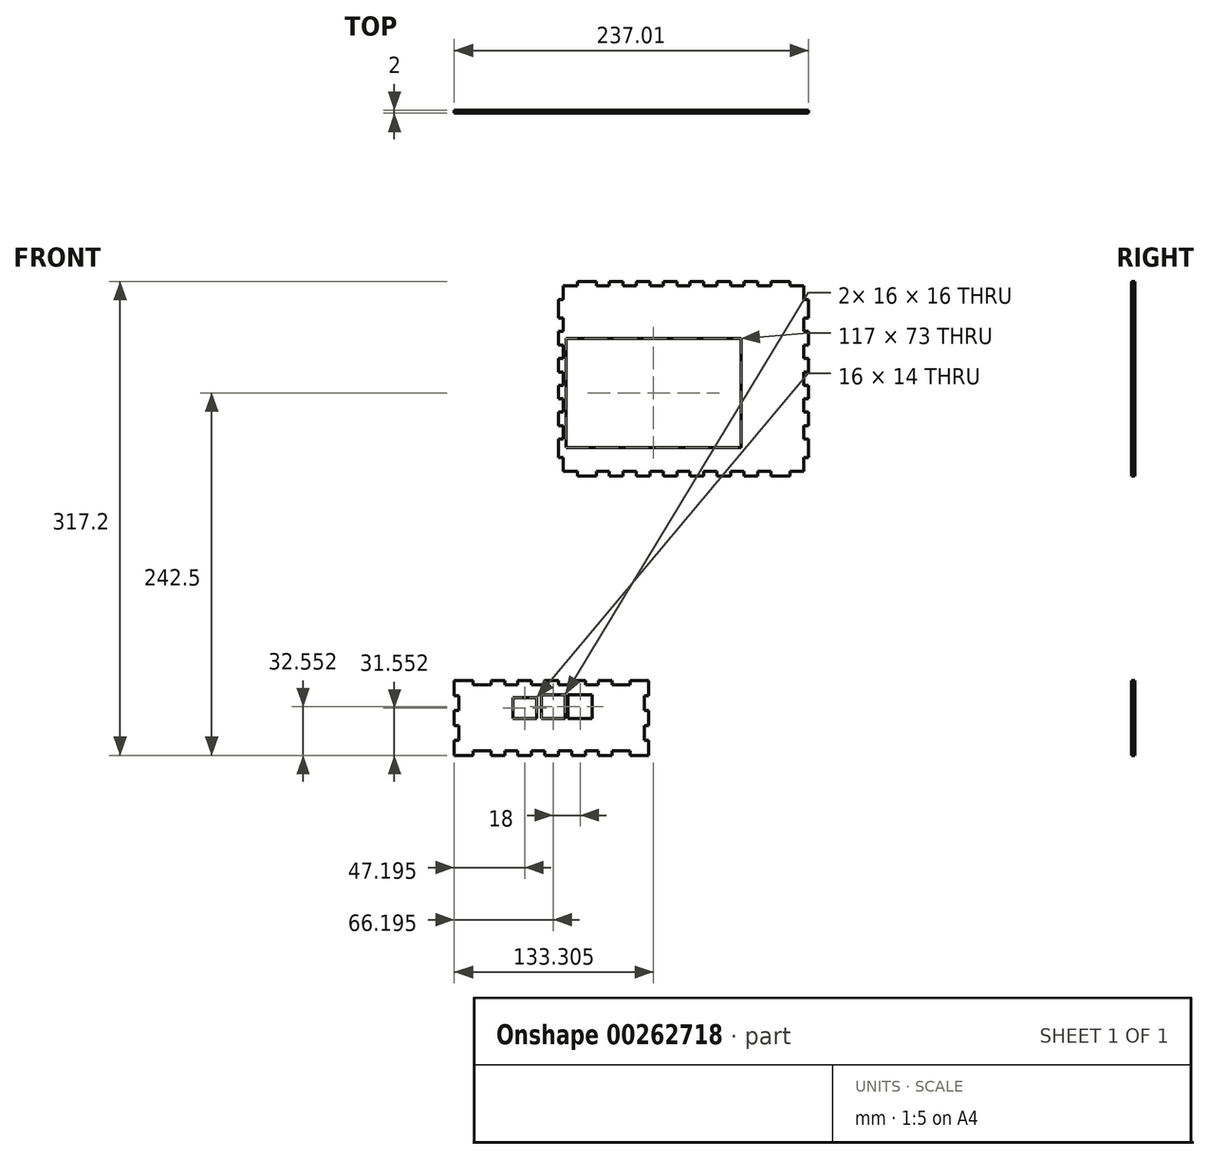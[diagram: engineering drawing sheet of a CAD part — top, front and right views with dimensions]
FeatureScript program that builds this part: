
annotation { "Feature Type Name" : "Feature", "Feature Type Description" : "" }
export const myFeature = defineFeature(function(context is Context, id is Id, definition is map)
    precondition{}
    {
        {
            var Q0;
            Q0=qCreatedBy(makeId("Front.planeOp"),FACE);
            var sketch = newSketch(context, id + "F0", { "sketchPlane" : qUnion([Q0])});
            skLineSegment(sketch, "E0.bottom", {"start": v(-364.73, 294.66) * mm, "end": v(-247.73, 294.66) * mm});
            skLineSegment(sketch, "E0.top", {"start": v(-364.73, 221.66) * mm, "end": v(-247.73, 221.66) * mm});
            skLineSegment(sketch, "E0.left", {"start": v(-364.73, 294.66) * mm, "end": v(-364.73, 221.66) * mm});
            skLineSegment(sketch, "E0.right", {"start": v(-247.73, 294.66) * mm, "end": v(-247.73, 221.66) * mm});
            skLineSegment(sketch, "E1.bottom", {"start": v(-103.23, 148.82) * mm, "end": v(61.85, 148.82) * mm});
            skLineSegment(sketch, "E1.top", {"start": v(-103.23, 18.82) * mm, "end": v(61.85, 18.82) * mm});
            skLineSegment(sketch, "E1.left", {"start": v(-103.23, 148.82) * mm, "end": v(-103.23, 18.82) * mm});
            skLineSegment(sketch, "E1.right", {"start": v(61.85, 148.82) * mm, "end": v(61.85, 18.82) * mm});
            skLineSegment(sketch, "E2", {"start": v(-298.1, 53.2) * mm, "end": v(-285.64, 53.2) * mm});
            skLineSegment(sketch, "E3", {"start": v(-285.64, 53.2) * mm, "end": v(-285.64, 50.2) * mm});
            skLineSegment(sketch, "E4", {"start": v(-285.64, 50.2) * mm, "end": v(-273.6, 50.2) * mm});
            skLineSegment(sketch, "E5", {"start": v(-273.6, 50.2) * mm, "end": v(-273.6, 53.2) * mm});
            skLineSegment(sketch, "E6", {"start": v(-273.6, 53.2) * mm, "end": v(-264.4, 53.2) * mm});
            skLineSegment(sketch, "E7", {"start": v(-264.4, 53.2) * mm, "end": v(-264.4, 50.2) * mm});
            skLineSegment(sketch, "E8", {"start": v(-264.4, 50.2) * mm, "end": v(-255.6, 50.2) * mm});
            skLineSegment(sketch, "E9", {"start": v(-255.6, 50.2) * mm, "end": v(-255.6, 53.2) * mm});
            skLineSegment(sketch, "E10", {"start": v(-255.6, 53.2) * mm, "end": v(-246.4, 53.2) * mm});
            skLineSegment(sketch, "E11", {"start": v(-246.4, 53.2) * mm, "end": v(-246.4, 50.2) * mm});
            skLineSegment(sketch, "E12", {"start": v(-246.4, 50.2) * mm, "end": v(-237.6, 50.2) * mm});
            skLineSegment(sketch, "E13", {"start": v(-237.6, 50.2) * mm, "end": v(-237.6, 53.2) * mm});
            skLineSegment(sketch, "E14", {"start": v(-237.6, 53.2) * mm, "end": v(-228.4, 53.2) * mm});
            skLineSegment(sketch, "E15", {"start": v(-228.4, 53.2) * mm, "end": v(-228.4, 50.2) * mm});
            skLineSegment(sketch, "E16", {"start": v(-228.4, 50.2) * mm, "end": v(-219.6, 50.2) * mm});
            skLineSegment(sketch, "E17", {"start": v(-219.6, 50.2) * mm, "end": v(-219.6, 53.2) * mm});
            skLineSegment(sketch, "E18", {"start": v(-219.6, 53.2) * mm, "end": v(-210.4, 53.2) * mm});
            skLineSegment(sketch, "E19", {"start": v(-210.4, 53.2) * mm, "end": v(-210.4, 50.2) * mm});
            skLineSegment(sketch, "E20", {"start": v(-210.4, 50.2) * mm, "end": v(-201.6, 50.2) * mm});
            skLineSegment(sketch, "E21", {"start": v(-201.6, 50.2) * mm, "end": v(-201.6, 53.2) * mm});
            skLineSegment(sketch, "E22", {"start": v(-201.6, 53.2) * mm, "end": v(-192.4, 53.2) * mm});
            skLineSegment(sketch, "E23", {"start": v(-192.4, 53.2) * mm, "end": v(-192.4, 50.2) * mm});
            skLineSegment(sketch, "E24", {"start": v(-192.4, 50.2) * mm, "end": v(-180.34, 50.2) * mm});
            skLineSegment(sketch, "E25", {"start": v(-180.34, 50.2) * mm, "end": v(-180.34, 53.2) * mm});
            skLineSegment(sketch, "E26", {"start": v(-180.34, 53.2) * mm, "end": v(-167.9, 53.2) * mm});
            skLineSegment(sketch, "E27", {"start": v(-167.9, 53.2) * mm, "end": v(-167.9, 43) * mm});
            skLineSegment(sketch, "E28", {"start": v(-167.9, 43) * mm, "end": v(-170.9, 43) * mm});
            skLineSegment(sketch, "E29", {"start": v(-170.9, 43) * mm, "end": v(-170.9, 33.2) * mm});
            skLineSegment(sketch, "E30", {"start": v(-170.9, 33.2) * mm, "end": v(-167.9, 33.2) * mm});
            skLineSegment(sketch, "E31", {"start": v(-167.9, 33.2) * mm, "end": v(-167.9, 23) * mm});
            skLineSegment(sketch, "E32", {"start": v(-167.9, 23) * mm, "end": v(-170.9, 23) * mm});
            skLineSegment(sketch, "E33", {"start": v(-170.9, 23) * mm, "end": v(-170.9, 13.2) * mm});
            skLineSegment(sketch, "E34", {"start": v(-170.9, 13.2) * mm, "end": v(-167.9, 13.2) * mm});
            skLineSegment(sketch, "E35", {"start": v(-167.9, 13.2) * mm, "end": v(-167.9, 3) * mm});
            skLineSegment(sketch, "E36", {"start": v(-167.9, 3) * mm, "end": v(-180.34, 3) * mm});
            skLineSegment(sketch, "E37", {"start": v(-180.34, 3) * mm, "end": v(-180.34, 6) * mm});
            skLineSegment(sketch, "E38", {"start": v(-180.34, 6) * mm, "end": v(-192.4, 6) * mm});
            skLineSegment(sketch, "E39", {"start": v(-192.4, 6) * mm, "end": v(-192.4, 3) * mm});
            skLineSegment(sketch, "E40", {"start": v(-192.4, 3) * mm, "end": v(-201.6, 3) * mm});
            skLineSegment(sketch, "E41", {"start": v(-201.6, 3) * mm, "end": v(-201.6, 6) * mm});
            skLineSegment(sketch, "E42", {"start": v(-201.6, 6) * mm, "end": v(-210.4, 6) * mm});
            skLineSegment(sketch, "E43", {"start": v(-210.4, 6) * mm, "end": v(-210.4, 3) * mm});
            skLineSegment(sketch, "E44", {"start": v(-210.4, 3) * mm, "end": v(-219.6, 3) * mm});
            skLineSegment(sketch, "E45", {"start": v(-219.6, 3) * mm, "end": v(-219.6, 6) * mm});
            skLineSegment(sketch, "E46", {"start": v(-219.6, 6) * mm, "end": v(-228.4, 6) * mm});
            skLineSegment(sketch, "E47", {"start": v(-228.4, 6) * mm, "end": v(-228.4, 3) * mm});
            skLineSegment(sketch, "E48", {"start": v(-228.4, 3) * mm, "end": v(-237.6, 3) * mm});
            skLineSegment(sketch, "E49", {"start": v(-237.6, 3) * mm, "end": v(-237.6, 6) * mm});
            skLineSegment(sketch, "E50", {"start": v(-237.6, 6) * mm, "end": v(-246.4, 6) * mm});
            skLineSegment(sketch, "E51", {"start": v(-246.4, 6) * mm, "end": v(-246.4, 3) * mm});
            skLineSegment(sketch, "E52", {"start": v(-246.4, 3) * mm, "end": v(-255.6, 3) * mm});
            skLineSegment(sketch, "E53", {"start": v(-255.6, 3) * mm, "end": v(-255.6, 6) * mm});
            skLineSegment(sketch, "E54", {"start": v(-255.6, 6) * mm, "end": v(-264.4, 6) * mm});
            skLineSegment(sketch, "E55", {"start": v(-264.4, 6) * mm, "end": v(-264.4, 3) * mm});
            skLineSegment(sketch, "E56", {"start": v(-264.4, 3) * mm, "end": v(-273.6, 3) * mm});
            skLineSegment(sketch, "E57", {"start": v(-273.6, 3) * mm, "end": v(-273.6, 6) * mm});
            skLineSegment(sketch, "E58", {"start": v(-273.6, 6) * mm, "end": v(-285.64, 6) * mm});
            skLineSegment(sketch, "E59", {"start": v(-285.64, 6) * mm, "end": v(-285.64, 3) * mm});
            skLineSegment(sketch, "E60", {"start": v(-285.64, 3) * mm, "end": v(-298.1, 3) * mm});
            skLineSegment(sketch, "E61", {"start": v(-298.1, 3) * mm, "end": v(-298.1, 13.2) * mm});
            skLineSegment(sketch, "E62", {"start": v(-298.1, 13.2) * mm, "end": v(-295.1, 13.2) * mm});
            skLineSegment(sketch, "E63", {"start": v(-295.1, 13.2) * mm, "end": v(-295.1, 23) * mm});
            skLineSegment(sketch, "E64", {"start": v(-295.1, 23) * mm, "end": v(-298.1, 23) * mm});
            skLineSegment(sketch, "E65", {"start": v(-298.1, 23) * mm, "end": v(-298.1, 33.2) * mm});
            skLineSegment(sketch, "E66", {"start": v(-298.1, 33.2) * mm, "end": v(-295.1, 33.2) * mm});
            skLineSegment(sketch, "E67", {"start": v(-295.1, 33.2) * mm, "end": v(-295.1, 43) * mm});
            skLineSegment(sketch, "E68", {"start": v(-295.1, 43) * mm, "end": v(-298.1, 43) * mm});
            skLineSegment(sketch, "E69", {"start": v(-298.1, 43) * mm, "end": v(-298.1, 53.2) * mm});
            skLineSegment(sketch, "E70", {"start": v(-225.28, 193) * mm, "end": v(-225.28, 202.25) * mm});
            skLineSegment(sketch, "E71", {"start": v(-225.28, 202.25) * mm, "end": v(-228.28, 202.25) * mm});
            skLineSegment(sketch, "E72", {"start": v(-228.28, 202.25) * mm, "end": v(-228.28, 214.7) * mm});
            skLineSegment(sketch, "E73", {"start": v(-228.28, 214.7) * mm, "end": v(-225.28, 214.7) * mm});
            skLineSegment(sketch, "E74", {"start": v(-225.28, 214.7) * mm, "end": v(-225.28, 223.5) * mm});
            skLineSegment(sketch, "E75", {"start": v(-225.28, 223.5) * mm, "end": v(-228.28, 223.5) * mm});
            skLineSegment(sketch, "E76", {"start": v(-228.28, 223.5) * mm, "end": v(-228.28, 232.7) * mm});
            skLineSegment(sketch, "E77", {"start": v(-228.28, 232.7) * mm, "end": v(-225.28, 232.7) * mm});
            skLineSegment(sketch, "E78", {"start": v(-225.28, 232.7) * mm, "end": v(-225.28, 241.5) * mm});
            skLineSegment(sketch, "E79", {"start": v(-225.28, 241.5) * mm, "end": v(-228.28, 241.5) * mm});
            skLineSegment(sketch, "E80", {"start": v(-228.28, 241.5) * mm, "end": v(-228.28, 250.7) * mm});
            skLineSegment(sketch, "E81", {"start": v(-228.28, 250.7) * mm, "end": v(-225.28, 250.7) * mm});
            skLineSegment(sketch, "E82", {"start": v(-225.28, 250.7) * mm, "end": v(-225.28, 259.5) * mm});
            skLineSegment(sketch, "E83", {"start": v(-225.28, 259.5) * mm, "end": v(-228.28, 259.5) * mm});
            skLineSegment(sketch, "E84", {"start": v(-228.28, 259.5) * mm, "end": v(-228.28, 268.7) * mm});
            skLineSegment(sketch, "E85", {"start": v(-228.28, 268.7) * mm, "end": v(-225.28, 268.7) * mm});
            skLineSegment(sketch, "E86", {"start": v(-225.28, 268.7) * mm, "end": v(-225.28, 277.5) * mm});
            skLineSegment(sketch, "E87", {"start": v(-225.28, 277.5) * mm, "end": v(-228.28, 277.5) * mm});
            skLineSegment(sketch, "E88", {"start": v(-228.28, 277.5) * mm, "end": v(-228.28, 286.7) * mm});
            skLineSegment(sketch, "E89", {"start": v(-228.28, 286.7) * mm, "end": v(-225.28, 286.7) * mm});
            skLineSegment(sketch, "E90", {"start": v(-225.28, 286.7) * mm, "end": v(-225.28, 295.5) * mm});
            skLineSegment(sketch, "E91", {"start": v(-225.28, 295.5) * mm, "end": v(-228.28, 295.5) * mm});
            skLineSegment(sketch, "E92", {"start": v(-228.28, 295.5) * mm, "end": v(-228.28, 307.95) * mm});
            skLineSegment(sketch, "E93", {"start": v(-228.28, 307.95) * mm, "end": v(-225.28, 307.95) * mm});
            skLineSegment(sketch, "E94", {"start": v(-225.28, 307.95) * mm, "end": v(-225.28, 317.2) * mm});
            skLineSegment(sketch, "E95", {"start": v(-225.28, 317.2) * mm, "end": v(-215.78, 317.2) * mm});
            skLineSegment(sketch, "E96", {"start": v(-215.78, 317.2) * mm, "end": v(-215.78, 320.2) * mm});
            skLineSegment(sketch, "E97", {"start": v(-215.78, 320.2) * mm, "end": v(-203.08, 320.2) * mm});
            skLineSegment(sketch, "E98", {"start": v(-203.08, 320.2) * mm, "end": v(-203.08, 317.2) * mm});
            skLineSegment(sketch, "E99", {"start": v(-203.08, 317.2) * mm, "end": v(-194.28, 317.2) * mm});
            skLineSegment(sketch, "E100", {"start": v(-194.28, 317.2) * mm, "end": v(-194.28, 320.2) * mm});
            skLineSegment(sketch, "E101", {"start": v(-194.28, 320.2) * mm, "end": v(-185.08, 320.2) * mm});
            skLineSegment(sketch, "E102", {"start": v(-185.08, 320.2) * mm, "end": v(-185.08, 317.2) * mm});
            skLineSegment(sketch, "E103", {"start": v(-185.08, 317.2) * mm, "end": v(-176.28, 317.2) * mm});
            skLineSegment(sketch, "E104", {"start": v(-176.28, 317.2) * mm, "end": v(-176.28, 320.2) * mm});
            skLineSegment(sketch, "E105", {"start": v(-176.28, 320.2) * mm, "end": v(-167.08, 320.2) * mm});
            skLineSegment(sketch, "E106", {"start": v(-167.08, 320.2) * mm, "end": v(-167.08, 317.2) * mm});
            skLineSegment(sketch, "E107", {"start": v(-167.08, 317.2) * mm, "end": v(-158.28, 317.2) * mm});
            skLineSegment(sketch, "E108", {"start": v(-158.28, 317.2) * mm, "end": v(-158.28, 320.2) * mm});
            skLineSegment(sketch, "E109", {"start": v(-158.28, 320.2) * mm, "end": v(-149.08, 320.2) * mm});
            skLineSegment(sketch, "E110", {"start": v(-149.08, 320.2) * mm, "end": v(-149.08, 317.2) * mm});
            skLineSegment(sketch, "E111", {"start": v(-149.08, 317.2) * mm, "end": v(-140.28, 317.2) * mm});
            skLineSegment(sketch, "E112", {"start": v(-140.28, 317.2) * mm, "end": v(-140.28, 320.2) * mm});
            skLineSegment(sketch, "E113", {"start": v(-140.28, 320.2) * mm, "end": v(-131.08, 320.2) * mm});
            skLineSegment(sketch, "E114", {"start": v(-131.08, 320.2) * mm, "end": v(-131.08, 317.2) * mm});
            skLineSegment(sketch, "E115", {"start": v(-131.08, 317.2) * mm, "end": v(-122.28, 317.2) * mm});
            skLineSegment(sketch, "E116", {"start": v(-122.28, 317.2) * mm, "end": v(-122.28, 320.2) * mm});
            skLineSegment(sketch, "E117", {"start": v(-122.28, 320.2) * mm, "end": v(-113.08, 320.2) * mm});
            skLineSegment(sketch, "E118", {"start": v(-113.08, 320.2) * mm, "end": v(-113.08, 317.2) * mm});
            skLineSegment(sketch, "E119", {"start": v(-113.08, 317.2) * mm, "end": v(-104.28, 317.2) * mm});
            skLineSegment(sketch, "E120", {"start": v(-104.28, 317.2) * mm, "end": v(-104.28, 320.2) * mm});
            skLineSegment(sketch, "E121", {"start": v(-104.28, 320.2) * mm, "end": v(-95.08, 320.2) * mm});
            skLineSegment(sketch, "E122", {"start": v(-95.08, 320.2) * mm, "end": v(-95.08, 317.2) * mm});
            skLineSegment(sketch, "E123", {"start": v(-95.08, 317.2) * mm, "end": v(-86.28, 317.2) * mm});
            skLineSegment(sketch, "E124", {"start": v(-86.28, 317.2) * mm, "end": v(-86.28, 320.2) * mm});
            skLineSegment(sketch, "E125", {"start": v(-86.28, 320.2) * mm, "end": v(-73.58, 320.2) * mm});
            skLineSegment(sketch, "E126", {"start": v(-73.58, 320.2) * mm, "end": v(-73.58, 317.2) * mm});
            skLineSegment(sketch, "E127", {"start": v(-73.58, 317.2) * mm, "end": v(-64.08, 317.2) * mm});
            skLineSegment(sketch, "E128", {"start": v(-64.08, 317.2) * mm, "end": v(-64.08, 307.95) * mm});
            skLineSegment(sketch, "E129", {"start": v(-64.08, 307.95) * mm, "end": v(-61.08, 307.95) * mm});
            skLineSegment(sketch, "E130", {"start": v(-61.08, 307.95) * mm, "end": v(-61.08, 295.5) * mm});
            skLineSegment(sketch, "E131", {"start": v(-61.08, 295.5) * mm, "end": v(-64.08, 295.5) * mm});
            skLineSegment(sketch, "E132", {"start": v(-64.08, 295.5) * mm, "end": v(-64.08, 286.7) * mm});
            skLineSegment(sketch, "E133", {"start": v(-64.08, 286.7) * mm, "end": v(-61.08, 286.7) * mm});
            skLineSegment(sketch, "E134", {"start": v(-61.08, 286.7) * mm, "end": v(-61.08, 277.5) * mm});
            skLineSegment(sketch, "E135", {"start": v(-61.08, 277.5) * mm, "end": v(-64.08, 277.5) * mm});
            skLineSegment(sketch, "E136", {"start": v(-64.08, 277.5) * mm, "end": v(-64.08, 268.7) * mm});
            skLineSegment(sketch, "E137", {"start": v(-64.08, 268.7) * mm, "end": v(-61.08, 268.7) * mm});
            skLineSegment(sketch, "E138", {"start": v(-61.08, 268.7) * mm, "end": v(-61.08, 259.5) * mm});
            skLineSegment(sketch, "E139", {"start": v(-61.08, 259.5) * mm, "end": v(-64.08, 259.5) * mm});
            skLineSegment(sketch, "E140", {"start": v(-64.08, 259.5) * mm, "end": v(-64.08, 250.7) * mm});
            skLineSegment(sketch, "E141", {"start": v(-64.08, 250.7) * mm, "end": v(-61.08, 250.7) * mm});
            skLineSegment(sketch, "E142", {"start": v(-61.08, 250.7) * mm, "end": v(-61.08, 241.5) * mm});
            skLineSegment(sketch, "E143", {"start": v(-61.08, 241.5) * mm, "end": v(-64.08, 241.5) * mm});
            skLineSegment(sketch, "E144", {"start": v(-64.08, 241.5) * mm, "end": v(-64.08, 232.7) * mm});
            skLineSegment(sketch, "E145", {"start": v(-64.08, 232.7) * mm, "end": v(-61.08, 232.7) * mm});
            skLineSegment(sketch, "E146", {"start": v(-61.08, 232.7) * mm, "end": v(-61.08, 223.5) * mm});
            skLineSegment(sketch, "E147", {"start": v(-61.08, 223.5) * mm, "end": v(-64.08, 223.5) * mm});
            skLineSegment(sketch, "E148", {"start": v(-64.08, 223.5) * mm, "end": v(-64.08, 214.7) * mm});
            skLineSegment(sketch, "E149", {"start": v(-64.08, 214.7) * mm, "end": v(-61.08, 214.7) * mm});
            skLineSegment(sketch, "E150", {"start": v(-61.08, 214.7) * mm, "end": v(-61.08, 202.25) * mm});
            skLineSegment(sketch, "E151", {"start": v(-61.08, 202.25) * mm, "end": v(-64.08, 202.25) * mm});
            skLineSegment(sketch, "E152", {"start": v(-64.08, 202.25) * mm, "end": v(-64.08, 193) * mm});
            skLineSegment(sketch, "E153", {"start": v(-64.08, 193) * mm, "end": v(-73.58, 193) * mm});
            skLineSegment(sketch, "E154", {"start": v(-73.58, 193) * mm, "end": v(-73.58, 190) * mm});
            skLineSegment(sketch, "E155", {"start": v(-73.58, 190) * mm, "end": v(-86.28, 190) * mm});
            skLineSegment(sketch, "E156", {"start": v(-86.28, 190) * mm, "end": v(-86.28, 193) * mm});
            skLineSegment(sketch, "E157", {"start": v(-86.28, 193) * mm, "end": v(-95.08, 193) * mm});
            skLineSegment(sketch, "E158", {"start": v(-95.08, 193) * mm, "end": v(-95.08, 190) * mm});
            skLineSegment(sketch, "E159", {"start": v(-95.08, 190) * mm, "end": v(-104.28, 190) * mm});
            skLineSegment(sketch, "E160", {"start": v(-104.28, 190) * mm, "end": v(-104.28, 193) * mm});
            skLineSegment(sketch, "E161", {"start": v(-104.28, 193) * mm, "end": v(-113.08, 193) * mm});
            skLineSegment(sketch, "E162", {"start": v(-113.08, 193) * mm, "end": v(-113.08, 190) * mm});
            skLineSegment(sketch, "E163", {"start": v(-113.08, 190) * mm, "end": v(-122.28, 190) * mm});
            skLineSegment(sketch, "E164", {"start": v(-122.28, 190) * mm, "end": v(-122.28, 193) * mm});
            skLineSegment(sketch, "E165", {"start": v(-122.28, 193) * mm, "end": v(-131.08, 193) * mm});
            skLineSegment(sketch, "E166", {"start": v(-131.08, 193) * mm, "end": v(-131.08, 190) * mm});
            skLineSegment(sketch, "E167", {"start": v(-131.08, 190) * mm, "end": v(-140.28, 190) * mm});
            skLineSegment(sketch, "E168", {"start": v(-140.28, 190) * mm, "end": v(-140.28, 193) * mm});
            skLineSegment(sketch, "E169", {"start": v(-140.28, 193) * mm, "end": v(-149.08, 193) * mm});
            skLineSegment(sketch, "E170", {"start": v(-149.08, 193) * mm, "end": v(-149.08, 190) * mm});
            skLineSegment(sketch, "E171", {"start": v(-149.08, 190) * mm, "end": v(-158.28, 190) * mm});
            skLineSegment(sketch, "E172", {"start": v(-158.28, 190) * mm, "end": v(-158.28, 193) * mm});
            skLineSegment(sketch, "E173", {"start": v(-158.28, 193) * mm, "end": v(-167.08, 193) * mm});
            skLineSegment(sketch, "E174", {"start": v(-167.08, 193) * mm, "end": v(-167.08, 190) * mm});
            skLineSegment(sketch, "E175", {"start": v(-167.08, 190) * mm, "end": v(-176.28, 190) * mm});
            skLineSegment(sketch, "E176", {"start": v(-176.28, 190) * mm, "end": v(-176.28, 193) * mm});
            skLineSegment(sketch, "E177", {"start": v(-176.28, 193) * mm, "end": v(-185.08, 193) * mm});
            skLineSegment(sketch, "E178", {"start": v(-185.08, 193) * mm, "end": v(-185.08, 190) * mm});
            skLineSegment(sketch, "E179", {"start": v(-185.08, 190) * mm, "end": v(-194.28, 190) * mm});
            skLineSegment(sketch, "E180", {"start": v(-194.28, 190) * mm, "end": v(-194.28, 193) * mm});
            skLineSegment(sketch, "E181", {"start": v(-194.28, 193) * mm, "end": v(-203.08, 193) * mm});
            skLineSegment(sketch, "E182", {"start": v(-203.08, 193) * mm, "end": v(-203.08, 190) * mm});
            skLineSegment(sketch, "E183", {"start": v(-203.08, 190) * mm, "end": v(-215.78, 190) * mm});
            skLineSegment(sketch, "E184", {"start": v(-215.78, 190) * mm, "end": v(-215.78, 193) * mm});
            skLineSegment(sketch, "E185", {"start": v(-215.78, 193) * mm, "end": v(-225.28, 193) * mm});
            skSolve(sketch);
        }
        {
            var Q0;
            Q0=makeQuery(id+"F0.imprint","IMPRINT",FACE,{"disambiguationData":[TD([[makeQuery(id+"F0.imprint","IMPRINT",EDGE,{"derivedFrom":sQuery(id+"F0.wireOp",EDGE,"E2")}),-1.0]])]});
            extrude(context, id + "F1", {"entities" : qUnion([Q0]), "depth" : 2 * mm});
        }
        {
            var Q0;
            Q0=makeQuery(id+"F1.opExtrude","CAP_FACE",FACE,{"disambiguationData":[OSD([sQuery(id+"F0.wireOp",EDGE,"hxJf8HKQ-p9ka-9bFz-WKYr-CpA7BwELEQiu.bottom"),sQuery(id+"F0.wireOp",EDGE,"hxJf8HKQ-p9ka-9bFz-WKYr-CpA7BwELEQiu.top"),sQuery(id+"F0.wireOp",EDGE,"hxJf8HKQ-p9ka-9bFz-WKYr-CpA7BwELEQiu.left"),sQuery(id+"F0.wireOp",EDGE,"hxJf8HKQ-p9ka-9bFz-WKYr-CpA7BwELEQiu.right"),sQuery(id+"F0.wireOp",EDGE,"RHciWNRG-vZu2-GtGd-OA35-ko8ltujrmhC4.bottom"),sQuery(id+"F0.wireOp",EDGE,"RHciWNRG-vZu2-GtGd-OA35-ko8ltujrmhC4.top"),sQuery(id+"F0.wireOp",EDGE,"RHciWNRG-vZu2-GtGd-OA35-ko8ltujrmhC4.left"),sQuery(id+"F0.wireOp",EDGE,"RHciWNRG-vZu2-GtGd-OA35-ko8ltujrmhC4.right"),sQuery(id+"F0.wireOp",EDGE,"69cdf3ec-0ad8-47e8-a303-1712bac806e2.bottom"),sQuery(id+"F0.wireOp",EDGE,"69cdf3ec-0ad8-47e8-a303-1712bac806e2.top"),sQuery(id+"F0.wireOp",EDGE,"69cdf3ec-0ad8-47e8-a303-1712bac806e2.left"),sQuery(id+"F0.wireOp",EDGE,"69cdf3ec-0ad8-47e8-a303-1712bac806e2.right"),sQuery(id+"F0.wireOp",EDGE,"E2"),sQuery(id+"F0.wireOp",EDGE,"E3"),sQuery(id+"F0.wireOp",EDGE,"E4"),sQuery(id+"F0.wireOp",EDGE,"E5"),sQuery(id+"F0.wireOp",EDGE,"E6"),sQuery(id+"F0.wireOp",EDGE,"E7"),sQuery(id+"F0.wireOp",EDGE,"E8"),sQuery(id+"F0.wireOp",EDGE,"E9"),sQuery(id+"F0.wireOp",EDGE,"E10"),sQuery(id+"F0.wireOp",EDGE,"E11"),sQuery(id+"F0.wireOp",EDGE,"E12"),sQuery(id+"F0.wireOp",EDGE,"E13"),sQuery(id+"F0.wireOp",EDGE,"E14"),sQuery(id+"F0.wireOp",EDGE,"E15"),sQuery(id+"F0.wireOp",EDGE,"E16"),sQuery(id+"F0.wireOp",EDGE,"E17"),sQuery(id+"F0.wireOp",EDGE,"E18"),sQuery(id+"F0.wireOp",EDGE,"E19"),sQuery(id+"F0.wireOp",EDGE,"E20"),sQuery(id+"F0.wireOp",EDGE,"E21"),sQuery(id+"F0.wireOp",EDGE,"E22"),sQuery(id+"F0.wireOp",EDGE,"E23"),sQuery(id+"F0.wireOp",EDGE,"E24"),sQuery(id+"F0.wireOp",EDGE,"E25"),sQuery(id+"F0.wireOp",EDGE,"E26"),sQuery(id+"F0.wireOp",EDGE,"E27"),sQuery(id+"F0.wireOp",EDGE,"E28"),sQuery(id+"F0.wireOp",EDGE,"E29"),sQuery(id+"F0.wireOp",EDGE,"E30"),sQuery(id+"F0.wireOp",EDGE,"E31"),sQuery(id+"F0.wireOp",EDGE,"E32"),sQuery(id+"F0.wireOp",EDGE,"E33"),sQuery(id+"F0.wireOp",EDGE,"E34"),sQuery(id+"F0.wireOp",EDGE,"E35"),sQuery(id+"F0.wireOp",EDGE,"E36"),sQuery(id+"F0.wireOp",EDGE,"E37"),sQuery(id+"F0.wireOp",EDGE,"E38"),sQuery(id+"F0.wireOp",EDGE,"E39"),sQuery(id+"F0.wireOp",EDGE,"E40"),sQuery(id+"F0.wireOp",EDGE,"E41"),sQuery(id+"F0.wireOp",EDGE,"E42"),sQuery(id+"F0.wireOp",EDGE,"E43"),sQuery(id+"F0.wireOp",EDGE,"E44"),sQuery(id+"F0.wireOp",EDGE,"E45"),sQuery(id+"F0.wireOp",EDGE,"E46"),sQuery(id+"F0.wireOp",EDGE,"E47"),sQuery(id+"F0.wireOp",EDGE,"E48"),sQuery(id+"F0.wireOp",EDGE,"E49"),sQuery(id+"F0.wireOp",EDGE,"E50"),sQuery(id+"F0.wireOp",EDGE,"E51"),sQuery(id+"F0.wireOp",EDGE,"E52"),sQuery(id+"F0.wireOp",EDGE,"E53"),sQuery(id+"F0.wireOp",EDGE,"E54"),sQuery(id+"F0.wireOp",EDGE,"E55"),sQuery(id+"F0.wireOp",EDGE,"E56"),sQuery(id+"F0.wireOp",EDGE,"E57"),sQuery(id+"F0.wireOp",EDGE,"E58"),sQuery(id+"F0.wireOp",EDGE,"E59"),sQuery(id+"F0.wireOp",EDGE,"E60"),sQuery(id+"F0.wireOp",EDGE,"E61"),sQuery(id+"F0.wireOp",EDGE,"E62"),sQuery(id+"F0.wireOp",EDGE,"E63"),sQuery(id+"F0.wireOp",EDGE,"E64"),sQuery(id+"F0.wireOp",EDGE,"E65"),sQuery(id+"F0.wireOp",EDGE,"E66"),sQuery(id+"F0.wireOp",EDGE,"E67"),sQuery(id+"F0.wireOp",EDGE,"E68"),sQuery(id+"F0.wireOp",EDGE,"E69")])],"isStart":false});
            var sketch = newSketch(context, id + "F2", { "sketchPlane" : qUnion([Q0])});
            skLineSegment(sketch, "E186.bottom", {"start": v(-78.01, 115.1) * mm, "end": v(43.27, 115.1) * mm});
            skLineSegment(sketch, "E186.top", {"start": v(-78.01, 37.3) * mm, "end": v(43.27, 37.3) * mm});
            skLineSegment(sketch, "E186.left", {"start": v(-78.01, 115.1) * mm, "end": v(-78.01, 37.3) * mm});
            skLineSegment(sketch, "E186.right", {"start": v(43.27, 115.1) * mm, "end": v(43.27, 37.3) * mm});
            skLineSegment(sketch, "E187.bottom", {"start": v(-78.36, 148.8) * mm, "end": v(81.64, 148.8) * mm});
            skLineSegment(sketch, "E187.top", {"start": v(-78.36, 18.8) * mm, "end": v(81.64, 18.8) * mm});
            skLineSegment(sketch, "E187.left", {"start": v(-78.36, 148.8) * mm, "end": v(-78.36, 18.8) * mm});
            skLineSegment(sketch, "E187.right", {"start": v(81.64, 148.8) * mm, "end": v(81.64, 18.8) * mm});
            skLineSegment(sketch, "E188.bottom", {"start": v(-78.36, 140.34) * mm, "end": v(-81.78, 140.34) * mm});
            skLineSegment(sketch, "E188.top", {"start": v(-78.36, 124.37) * mm, "end": v(-81.78, 124.37) * mm});
            skLineSegment(sketch, "E188.left", {"start": v(-78.36, 140.34) * mm, "end": v(-78.36, 124.37) * mm});
            skLineSegment(sketch, "E188.right", {"start": v(-81.78, 140.34) * mm, "end": v(-81.78, 124.37) * mm});
            skLineSegment(sketch, "E189.bottom", {"start": v(-239.9, 43.55) * mm, "end": v(-223.9, 43.55) * mm});
            skLineSegment(sketch, "E189.top", {"start": v(-239.9, 27.55) * mm, "end": v(-223.9, 27.55) * mm});
            skLineSegment(sketch, "E189.left", {"start": v(-239.9, 43.55) * mm, "end": v(-239.9, 27.55) * mm});
            skLineSegment(sketch, "E189.right", {"start": v(-223.9, 43.55) * mm, "end": v(-223.9, 27.55) * mm});
            skLineSegment(sketch, "E190.bottom", {"start": v(-258.9, 41.55) * mm, "end": v(-242.9, 41.55) * mm});
            skLineSegment(sketch, "E190.top", {"start": v(-258.9, 27.55) * mm, "end": v(-242.9, 27.55) * mm});
            skLineSegment(sketch, "E190.left", {"start": v(-258.9, 41.55) * mm, "end": v(-258.9, 27.55) * mm});
            skLineSegment(sketch, "E190.right", {"start": v(-242.9, 41.55) * mm, "end": v(-242.9, 27.55) * mm});
            skLineSegment(sketch, "E191.bottom", {"start": v(-221.9, 43.55) * mm, "end": v(-205.9, 43.55) * mm});
            skLineSegment(sketch, "E191.top", {"start": v(-221.9, 27.55) * mm, "end": v(-205.9, 27.55) * mm});
            skLineSegment(sketch, "E191.left", {"start": v(-221.9, 43.55) * mm, "end": v(-221.9, 27.55) * mm});
            skLineSegment(sketch, "E191.right", {"start": v(-205.9, 43.55) * mm, "end": v(-205.9, 27.55) * mm});
            skLineSegment(sketch, "E192", {"start": v(-186.9, 42.25) * mm, "end": v(-186.9, 36.29) * mm});
            skSolve(sketch);
        }
        {
            var Q0;
            Q0=makeQuery(id+"F0.imprint","IMPRINT",FACE,{"disambiguationData":[TD([[makeQuery(id+"F0.imprint","IMPRINT",EDGE,{"derivedFrom":sQuery(id+"F0.wireOp",EDGE,"E70")}),-1.0]])]});
            extrude(context, id + "F3", {"entities" : qUnion([Q0]), "depth" : 2 * mm});
        }
        {
            var Q0;
            Q0=makeQuery(id+"F3.opExtrude","CAP_FACE",FACE,{"disambiguationData":[OSD([sQuery(id+"F0.wireOp",EDGE,"E70"),sQuery(id+"F0.wireOp",EDGE,"E71"),sQuery(id+"F0.wireOp",EDGE,"E72"),sQuery(id+"F0.wireOp",EDGE,"E73"),sQuery(id+"F0.wireOp",EDGE,"E74"),sQuery(id+"F0.wireOp",EDGE,"E75"),sQuery(id+"F0.wireOp",EDGE,"E76"),sQuery(id+"F0.wireOp",EDGE,"E77"),sQuery(id+"F0.wireOp",EDGE,"E78"),sQuery(id+"F0.wireOp",EDGE,"E79"),sQuery(id+"F0.wireOp",EDGE,"E80"),sQuery(id+"F0.wireOp",EDGE,"E81"),sQuery(id+"F0.wireOp",EDGE,"E82"),sQuery(id+"F0.wireOp",EDGE,"E83"),sQuery(id+"F0.wireOp",EDGE,"E84"),sQuery(id+"F0.wireOp",EDGE,"E85"),sQuery(id+"F0.wireOp",EDGE,"E86"),sQuery(id+"F0.wireOp",EDGE,"E87"),sQuery(id+"F0.wireOp",EDGE,"E88"),sQuery(id+"F0.wireOp",EDGE,"E89"),sQuery(id+"F0.wireOp",EDGE,"E90"),sQuery(id+"F0.wireOp",EDGE,"E91"),sQuery(id+"F0.wireOp",EDGE,"E92"),sQuery(id+"F0.wireOp",EDGE,"E93"),sQuery(id+"F0.wireOp",EDGE,"E94"),sQuery(id+"F0.wireOp",EDGE,"E95"),sQuery(id+"F0.wireOp",EDGE,"E96"),sQuery(id+"F0.wireOp",EDGE,"E97"),sQuery(id+"F0.wireOp",EDGE,"E98"),sQuery(id+"F0.wireOp",EDGE,"E99"),sQuery(id+"F0.wireOp",EDGE,"E100"),sQuery(id+"F0.wireOp",EDGE,"E101"),sQuery(id+"F0.wireOp",EDGE,"E102"),sQuery(id+"F0.wireOp",EDGE,"E103"),sQuery(id+"F0.wireOp",EDGE,"E104"),sQuery(id+"F0.wireOp",EDGE,"E105"),sQuery(id+"F0.wireOp",EDGE,"E106"),sQuery(id+"F0.wireOp",EDGE,"E107"),sQuery(id+"F0.wireOp",EDGE,"E108"),sQuery(id+"F0.wireOp",EDGE,"E109"),sQuery(id+"F0.wireOp",EDGE,"E110"),sQuery(id+"F0.wireOp",EDGE,"E111"),sQuery(id+"F0.wireOp",EDGE,"E112"),sQuery(id+"F0.wireOp",EDGE,"E113"),sQuery(id+"F0.wireOp",EDGE,"E114"),sQuery(id+"F0.wireOp",EDGE,"E115"),sQuery(id+"F0.wireOp",EDGE,"E116"),sQuery(id+"F0.wireOp",EDGE,"E117"),sQuery(id+"F0.wireOp",EDGE,"E118"),sQuery(id+"F0.wireOp",EDGE,"E119"),sQuery(id+"F0.wireOp",EDGE,"E120"),sQuery(id+"F0.wireOp",EDGE,"E121"),sQuery(id+"F0.wireOp",EDGE,"E122"),sQuery(id+"F0.wireOp",EDGE,"E123"),sQuery(id+"F0.wireOp",EDGE,"E124"),sQuery(id+"F0.wireOp",EDGE,"E125"),sQuery(id+"F0.wireOp",EDGE,"E126"),sQuery(id+"F0.wireOp",EDGE,"E127"),sQuery(id+"F0.wireOp",EDGE,"E128"),sQuery(id+"F0.wireOp",EDGE,"E129"),sQuery(id+"F0.wireOp",EDGE,"E130"),sQuery(id+"F0.wireOp",EDGE,"E131"),sQuery(id+"F0.wireOp",EDGE,"E132"),sQuery(id+"F0.wireOp",EDGE,"E133"),sQuery(id+"F0.wireOp",EDGE,"E134"),sQuery(id+"F0.wireOp",EDGE,"E135"),sQuery(id+"F0.wireOp",EDGE,"E136"),sQuery(id+"F0.wireOp",EDGE,"E137"),sQuery(id+"F0.wireOp",EDGE,"E138"),sQuery(id+"F0.wireOp",EDGE,"E139"),sQuery(id+"F0.wireOp",EDGE,"E140"),sQuery(id+"F0.wireOp",EDGE,"E141"),sQuery(id+"F0.wireOp",EDGE,"E142"),sQuery(id+"F0.wireOp",EDGE,"E143"),sQuery(id+"F0.wireOp",EDGE,"E144"),sQuery(id+"F0.wireOp",EDGE,"E145"),sQuery(id+"F0.wireOp",EDGE,"E146"),sQuery(id+"F0.wireOp",EDGE,"E147"),sQuery(id+"F0.wireOp",EDGE,"E148"),sQuery(id+"F0.wireOp",EDGE,"E149"),sQuery(id+"F0.wireOp",EDGE,"E150"),sQuery(id+"F0.wireOp",EDGE,"E151"),sQuery(id+"F0.wireOp",EDGE,"E152"),sQuery(id+"F0.wireOp",EDGE,"E153"),sQuery(id+"F0.wireOp",EDGE,"E154"),sQuery(id+"F0.wireOp",EDGE,"E155"),sQuery(id+"F0.wireOp",EDGE,"E156"),sQuery(id+"F0.wireOp",EDGE,"E157"),sQuery(id+"F0.wireOp",EDGE,"E158"),sQuery(id+"F0.wireOp",EDGE,"E159"),sQuery(id+"F0.wireOp",EDGE,"E160"),sQuery(id+"F0.wireOp",EDGE,"E161"),sQuery(id+"F0.wireOp",EDGE,"E162"),sQuery(id+"F0.wireOp",EDGE,"E163"),sQuery(id+"F0.wireOp",EDGE,"E164"),sQuery(id+"F0.wireOp",EDGE,"E165"),sQuery(id+"F0.wireOp",EDGE,"E166"),sQuery(id+"F0.wireOp",EDGE,"E167"),sQuery(id+"F0.wireOp",EDGE,"E168"),sQuery(id+"F0.wireOp",EDGE,"E169"),sQuery(id+"F0.wireOp",EDGE,"E170"),sQuery(id+"F0.wireOp",EDGE,"E171"),sQuery(id+"F0.wireOp",EDGE,"E172"),sQuery(id+"F0.wireOp",EDGE,"E173"),sQuery(id+"F0.wireOp",EDGE,"E174"),sQuery(id+"F0.wireOp",EDGE,"E175"),sQuery(id+"F0.wireOp",EDGE,"E176"),sQuery(id+"F0.wireOp",EDGE,"E177"),sQuery(id+"F0.wireOp",EDGE,"E178"),sQuery(id+"F0.wireOp",EDGE,"E179"),sQuery(id+"F0.wireOp",EDGE,"E180"),sQuery(id+"F0.wireOp",EDGE,"E181"),sQuery(id+"F0.wireOp",EDGE,"E182"),sQuery(id+"F0.wireOp",EDGE,"E183"),sQuery(id+"F0.wireOp",EDGE,"E184"),sQuery(id+"F0.wireOp",EDGE,"E185")])],"isStart":false});
            var sketch = newSketch(context, id + "F4", { "sketchPlane" : qUnion([Q0])});
            skLineSegment(sketch, "E193.bottom", {"start": v(-223.28, 282) * mm, "end": v(-106.28, 282) * mm});
            skLineSegment(sketch, "E193.top", {"start": v(-223.28, 209) * mm, "end": v(-106.28, 209) * mm});
            skLineSegment(sketch, "E193.left", {"start": v(-223.28, 282) * mm, "end": v(-223.28, 209) * mm});
            skLineSegment(sketch, "E193.right", {"start": v(-106.28, 282) * mm, "end": v(-106.28, 209) * mm});
            skSolve(sketch);
        }
        {
            var Q0;
            Q0=makeQuery(id+"F4.imprint","IMPRINT",FACE,{"disambiguationData":[TD([[makeQuery(id+"F4.imprint","IMPRINT",EDGE,{"derivedFrom":sQuery(id+"F4.wireOp",EDGE,"E193.bottom")}),-1.0]])]});
            extrude(context, id + "F5", {"entities" : qUnion([Q0]), "operationType" : NewBodyOperationType.REMOVE, "oppositeDirection" : true, "depth" : 3 * mm});
        }
        {
            var Q0;
            Q0=makeQuery(id+"F2.imprint","IMPRINT",FACE,{"disambiguationData":[TD([[makeQuery(id+"F2.imprint","IMPRINT",EDGE,{"derivedFrom":sQuery(id+"F2.wireOp",EDGE,"E191.bottom")}),-1.0]])]});
            var Q1;
            Q1=makeQuery(id+"F2.imprint","IMPRINT",FACE,{"disambiguationData":[TD([[makeQuery(id+"F2.imprint","IMPRINT",EDGE,{"derivedFrom":sQuery(id+"F2.wireOp",EDGE,"E189.bottom")}),-1.0]])]});
            var Q2;
            Q2=makeQuery(id+"F2.imprint","IMPRINT",FACE,{"disambiguationData":[TD([[makeQuery(id+"F2.imprint","IMPRINT",EDGE,{"derivedFrom":sQuery(id+"F2.wireOp",EDGE,"E190.bottom")}),-1.0]])]});
            extrude(context, id + "F6", {"entities" : qUnion([Q0, Q1, Q2]), "operationType" : NewBodyOperationType.REMOVE, "oppositeDirection" : true, "depth" : 3 * mm});
        }
    });
